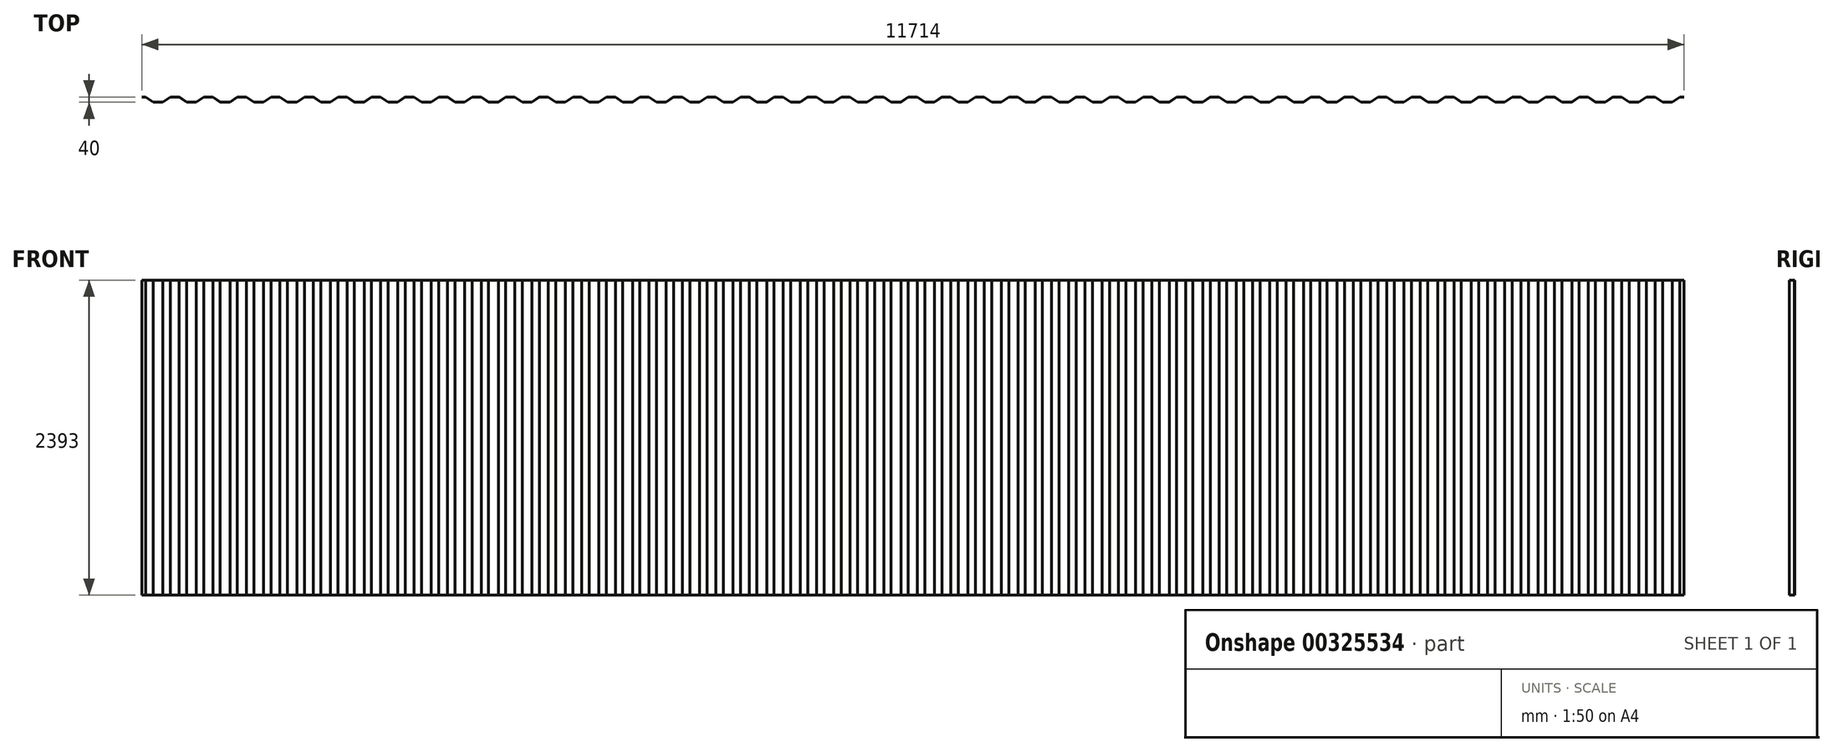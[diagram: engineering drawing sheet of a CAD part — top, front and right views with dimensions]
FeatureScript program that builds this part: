
annotation { "Feature Type Name" : "Feature", "Feature Type Description" : "" }
export const myFeature = defineFeature(function(context is Context, id is Id, definition is map)
    precondition{}
    {
        {
            var Q0;
            Q0=qCreatedBy(makeId("Top.planeOp"),FACE);
            var sketch = newSketch(context, id + "F0", { "sketchPlane" : qUnion([Q0])});
            skLineSegment(sketch, "E0", {"start": v(-32, 17.21) * mm, "end": v(-1.35, 17.21) * mm});
            skLineSegment(sketch, "E1", {"start": v(-1.35, 17.21) * mm, "end": v(55.04, -20.79) * mm});
            skLineSegment(sketch, "E2", {"start": v(55.04, -20.79) * mm, "end": v(127.96, -20.79) * mm});
            skLineSegment(sketch, "E3", {"start": v(127.96, -20.79) * mm, "end": v(184.35, 17.21) * mm});
            skLineSegment(sketch, "E4", {"start": v(184.35, 17.21) * mm, "end": v(253.44, 17.21) * mm});
            skLineSegment(sketch, "E5", {"start": v(253.44, 17.21) * mm, "end": v(309.83, -20.79) * mm});
            skLineSegment(sketch, "E6", {"start": v(309.83, -20.79) * mm, "end": v(382.74, -20.79) * mm});
            skLineSegment(sketch, "E7", {"start": v(382.74, -20.79) * mm, "end": v(439.14, 17.21) * mm});
            skLineSegment(sketch, "E8", {"start": v(439.14, 17.21) * mm, "end": v(508.22, 17.21) * mm});
            skLineSegment(sketch, "E9", {"start": v(508.22, 17.21) * mm, "end": v(564.61, -20.79) * mm});
            skLineSegment(sketch, "E10", {"start": v(564.61, -20.79) * mm, "end": v(637.53, -20.79) * mm});
            skLineSegment(sketch, "E11", {"start": v(637.53, -20.79) * mm, "end": v(693.92, 17.21) * mm});
            skLineSegment(sketch, "E12", {"start": v(693.92, 17.21) * mm, "end": v(763, 17.21) * mm});
            skLineSegment(sketch, "E13", {"start": v(763, 17.21) * mm, "end": v(819.4, -20.79) * mm});
            skLineSegment(sketch, "E14", {"start": v(819.4, -20.79) * mm, "end": v(892.31, -20.79) * mm});
            skLineSegment(sketch, "E15", {"start": v(892.31, -20.79) * mm, "end": v(948.7, 17.21) * mm});
            skLineSegment(sketch, "E16", {"start": v(948.7, 17.21) * mm, "end": v(1017.79, 17.21) * mm});
            skLineSegment(sketch, "E17", {"start": v(1017.79, 17.21) * mm, "end": v(1074.18, -20.79) * mm});
            skLineSegment(sketch, "E18", {"start": v(1074.18, -20.79) * mm, "end": v(1147.1, -20.79) * mm});
            skLineSegment(sketch, "E19", {"start": v(1147.1, -20.79) * mm, "end": v(1203.48, 17.21) * mm});
            skLineSegment(sketch, "E20", {"start": v(1203.48, 17.21) * mm, "end": v(1272.57, 17.21) * mm});
            skLineSegment(sketch, "E21", {"start": v(1272.57, 17.21) * mm, "end": v(1328.96, -20.79) * mm});
            skLineSegment(sketch, "E22", {"start": v(1328.96, -20.79) * mm, "end": v(1401.88, -20.79) * mm});
            skLineSegment(sketch, "E23", {"start": v(1401.88, -20.79) * mm, "end": v(1458.27, 17.21) * mm});
            skLineSegment(sketch, "E24", {"start": v(1458.27, 17.21) * mm, "end": v(1527.35, 17.21) * mm});
            skLineSegment(sketch, "E25", {"start": v(1527.35, 17.21) * mm, "end": v(1583.74, -20.79) * mm});
            skLineSegment(sketch, "E26", {"start": v(1583.74, -20.79) * mm, "end": v(1656.66, -20.79) * mm});
            skLineSegment(sketch, "E27", {"start": v(1656.66, -20.79) * mm, "end": v(1713.05, 17.21) * mm});
            skLineSegment(sketch, "E28", {"start": v(1713.05, 17.21) * mm, "end": v(1782.13, 17.21) * mm});
            skLineSegment(sketch, "E29", {"start": v(1782.13, 17.21) * mm, "end": v(1838.53, -20.79) * mm});
            skLineSegment(sketch, "E30", {"start": v(1838.53, -20.79) * mm, "end": v(1911.44, -20.79) * mm});
            skLineSegment(sketch, "E31", {"start": v(1911.44, -20.79) * mm, "end": v(1967.83, 17.21) * mm});
            skLineSegment(sketch, "E32", {"start": v(1967.83, 17.21) * mm, "end": v(2036.92, 17.21) * mm});
            skLineSegment(sketch, "E33", {"start": v(2036.92, 17.21) * mm, "end": v(2093.3, -20.79) * mm});
            skLineSegment(sketch, "E34", {"start": v(2093.3, -20.79) * mm, "end": v(2166.22, -20.79) * mm});
            skLineSegment(sketch, "E35", {"start": v(2166.22, -20.79) * mm, "end": v(2222.62, 17.21) * mm});
            skLineSegment(sketch, "E36", {"start": v(2222.62, 17.21) * mm, "end": v(2291.7, 17.21) * mm});
            skLineSegment(sketch, "E37", {"start": v(2291.7, 17.21) * mm, "end": v(2348.1, -20.79) * mm});
            skLineSegment(sketch, "E38", {"start": v(2348.1, -20.79) * mm, "end": v(2421, -20.79) * mm});
            skLineSegment(sketch, "E39", {"start": v(2421, -20.79) * mm, "end": v(2477.4, 17.21) * mm});
            skLineSegment(sketch, "E40", {"start": v(2477.4, 17.21) * mm, "end": v(2546.48, 17.21) * mm});
            skLineSegment(sketch, "E41", {"start": v(2546.48, 17.21) * mm, "end": v(2602.87, -20.79) * mm});
            skLineSegment(sketch, "E42", {"start": v(2602.87, -20.79) * mm, "end": v(2675.8, -20.79) * mm});
            skLineSegment(sketch, "E43", {"start": v(2675.8, -20.79) * mm, "end": v(2732.18, 17.21) * mm});
            skLineSegment(sketch, "E44", {"start": v(2732.18, 17.21) * mm, "end": v(2801.27, 17.21) * mm});
            skLineSegment(sketch, "E45", {"start": v(2801.27, 17.21) * mm, "end": v(2857.66, -20.79) * mm});
            skLineSegment(sketch, "E46", {"start": v(2857.66, -20.79) * mm, "end": v(2930.57, -20.79) * mm});
            skLineSegment(sketch, "E47", {"start": v(2930.57, -20.79) * mm, "end": v(2986.97, 17.21) * mm});
            skLineSegment(sketch, "E48", {"start": v(2986.97, 17.21) * mm, "end": v(3056.05, 17.21) * mm});
            skLineSegment(sketch, "E49", {"start": v(3056.05, 17.21) * mm, "end": v(3112.44, -20.79) * mm});
            skLineSegment(sketch, "E50", {"start": v(3112.44, -20.79) * mm, "end": v(3185.36, -20.79) * mm});
            skLineSegment(sketch, "E51", {"start": v(3185.36, -20.79) * mm, "end": v(3241.75, 17.21) * mm});
            skLineSegment(sketch, "E52", {"start": v(3241.75, 17.21) * mm, "end": v(3310.83, 17.21) * mm});
            skLineSegment(sketch, "E53", {"start": v(3310.83, 17.21) * mm, "end": v(3367.22, -20.79) * mm});
            skLineSegment(sketch, "E54", {"start": v(3367.22, -20.79) * mm, "end": v(3440.14, -20.79) * mm});
            skLineSegment(sketch, "E55", {"start": v(3440.14, -20.79) * mm, "end": v(3496.53, 17.21) * mm});
            skLineSegment(sketch, "E56", {"start": v(3496.53, 17.21) * mm, "end": v(3565.61, 17.21) * mm});
            skLineSegment(sketch, "E57", {"start": v(3565.61, 17.21) * mm, "end": v(3622, -20.79) * mm});
            skLineSegment(sketch, "E58", {"start": v(3622, -20.79) * mm, "end": v(3694.92, -20.79) * mm});
            skLineSegment(sketch, "E59", {"start": v(3694.92, -20.79) * mm, "end": v(3751.31, 17.21) * mm});
            skLineSegment(sketch, "E60", {"start": v(3751.31, 17.21) * mm, "end": v(3820.4, 17.21) * mm});
            skLineSegment(sketch, "E61", {"start": v(3820.4, 17.21) * mm, "end": v(3876.79, -20.79) * mm});
            skLineSegment(sketch, "E62", {"start": v(3876.79, -20.79) * mm, "end": v(3949.7, -20.79) * mm});
            skLineSegment(sketch, "E63", {"start": v(3949.7, -20.79) * mm, "end": v(4006.1, 17.21) * mm});
            skLineSegment(sketch, "E64", {"start": v(4006.1, 17.21) * mm, "end": v(4075.18, 17.21) * mm});
            skLineSegment(sketch, "E65", {"start": v(4075.18, 17.21) * mm, "end": v(4131.57, -20.79) * mm});
            skLineSegment(sketch, "E66", {"start": v(4131.57, -20.79) * mm, "end": v(4204.49, -20.79) * mm});
            skLineSegment(sketch, "E67", {"start": v(4204.49, -20.79) * mm, "end": v(4260.88, 17.21) * mm});
            skLineSegment(sketch, "E68", {"start": v(4260.88, 17.21) * mm, "end": v(4329.96, 17.21) * mm});
            skLineSegment(sketch, "E69", {"start": v(4329.96, 17.21) * mm, "end": v(4386.36, -20.79) * mm});
            skLineSegment(sketch, "E70", {"start": v(4386.36, -20.79) * mm, "end": v(4459.27, -20.79) * mm});
            skLineSegment(sketch, "E71", {"start": v(4459.27, -20.79) * mm, "end": v(4515.66, 17.21) * mm});
            skLineSegment(sketch, "E72", {"start": v(4515.66, 17.21) * mm, "end": v(4584.75, 17.21) * mm});
            skLineSegment(sketch, "E73", {"start": v(4584.75, 17.21) * mm, "end": v(4641.14, -20.79) * mm});
            skLineSegment(sketch, "E74", {"start": v(4641.14, -20.79) * mm, "end": v(4714.05, -20.79) * mm});
            skLineSegment(sketch, "E75", {"start": v(4714.05, -20.79) * mm, "end": v(4770.45, 17.21) * mm});
            skLineSegment(sketch, "E76", {"start": v(4770.45, 17.21) * mm, "end": v(4839.53, 17.21) * mm});
            skLineSegment(sketch, "E77", {"start": v(4839.53, 17.21) * mm, "end": v(4895.92, -20.79) * mm});
            skLineSegment(sketch, "E78", {"start": v(4895.92, -20.79) * mm, "end": v(4968.84, -20.79) * mm});
            skLineSegment(sketch, "E79", {"start": v(4968.84, -20.79) * mm, "end": v(5025.23, 17.21) * mm});
            skLineSegment(sketch, "E80", {"start": v(5025.23, 17.21) * mm, "end": v(5094.31, 17.21) * mm});
            skLineSegment(sketch, "E81", {"start": v(5094.31, 17.21) * mm, "end": v(5150.7, -20.79) * mm});
            skLineSegment(sketch, "E82", {"start": v(5150.7, -20.79) * mm, "end": v(5223.62, -20.79) * mm});
            skLineSegment(sketch, "E83", {"start": v(5223.62, -20.79) * mm, "end": v(5280.01, 17.21) * mm});
            skLineSegment(sketch, "E84", {"start": v(5280.01, 17.21) * mm, "end": v(5349.1, 17.21) * mm});
            skLineSegment(sketch, "E85", {"start": v(5349.1, 17.21) * mm, "end": v(5405.49, -20.79) * mm});
            skLineSegment(sketch, "E86", {"start": v(5405.49, -20.79) * mm, "end": v(5478.4, -20.79) * mm});
            skLineSegment(sketch, "E87", {"start": v(5478.4, -20.79) * mm, "end": v(5534.8, 17.21) * mm});
            skLineSegment(sketch, "E88", {"start": v(5534.8, 17.21) * mm, "end": v(5603.88, 17.21) * mm});
            skLineSegment(sketch, "E89", {"start": v(5603.88, 17.21) * mm, "end": v(5660.27, -20.79) * mm});
            skLineSegment(sketch, "E90", {"start": v(5660.27, -20.79) * mm, "end": v(5733.19, -20.79) * mm});
            skLineSegment(sketch, "E91", {"start": v(5733.19, -20.79) * mm, "end": v(5789.58, 17.21) * mm});
            skLineSegment(sketch, "E92", {"start": v(5789.58, 17.21) * mm, "end": v(5858.66, 17.21) * mm});
            skLineSegment(sketch, "E93", {"start": v(5858.66, 17.21) * mm, "end": v(5915.05, -20.79) * mm});
            skLineSegment(sketch, "E94", {"start": v(5915.05, -20.79) * mm, "end": v(5987.97, -20.79) * mm});
            skLineSegment(sketch, "E95", {"start": v(5987.97, -20.79) * mm, "end": v(6044.36, 17.21) * mm});
            skLineSegment(sketch, "E96", {"start": v(6044.36, 17.21) * mm, "end": v(6113.44, 17.21) * mm});
            skLineSegment(sketch, "E97", {"start": v(6113.44, 17.21) * mm, "end": v(6169.84, -20.79) * mm});
            skLineSegment(sketch, "E98", {"start": v(6169.84, -20.79) * mm, "end": v(6242.75, -20.79) * mm});
            skLineSegment(sketch, "E99", {"start": v(6242.75, -20.79) * mm, "end": v(6299.14, 17.21) * mm});
            skLineSegment(sketch, "E100", {"start": v(6299.14, 17.21) * mm, "end": v(6368.23, 17.21) * mm});
            skLineSegment(sketch, "E101", {"start": v(6368.23, 17.21) * mm, "end": v(6424.62, -20.79) * mm});
            skLineSegment(sketch, "E102", {"start": v(6424.62, -20.79) * mm, "end": v(6497.54, -20.79) * mm});
            skLineSegment(sketch, "E103", {"start": v(6497.54, -20.79) * mm, "end": v(6553.93, 17.21) * mm});
            skLineSegment(sketch, "E104", {"start": v(6553.93, 17.21) * mm, "end": v(6623.01, 17.21) * mm});
            skLineSegment(sketch, "E105", {"start": v(6623.01, 17.21) * mm, "end": v(6679.4, -20.79) * mm});
            skLineSegment(sketch, "E106", {"start": v(6679.4, -20.79) * mm, "end": v(6752.32, -20.79) * mm});
            skLineSegment(sketch, "E107", {"start": v(6752.32, -20.79) * mm, "end": v(6808.71, 17.21) * mm});
            skLineSegment(sketch, "E108", {"start": v(6808.71, 17.21) * mm, "end": v(6877.8, 17.21) * mm});
            skLineSegment(sketch, "E109", {"start": v(6877.8, 17.21) * mm, "end": v(6934.19, -20.79) * mm});
            skLineSegment(sketch, "E110", {"start": v(6934.19, -20.79) * mm, "end": v(7007.1, -20.79) * mm});
            skLineSegment(sketch, "E111", {"start": v(7007.1, -20.79) * mm, "end": v(7063.5, 17.21) * mm});
            skLineSegment(sketch, "E112", {"start": v(7063.5, 17.21) * mm, "end": v(7132.58, 17.21) * mm});
            skLineSegment(sketch, "E113", {"start": v(7132.58, 17.21) * mm, "end": v(7188.97, -20.79) * mm});
            skLineSegment(sketch, "E114", {"start": v(7188.97, -20.79) * mm, "end": v(7261.88, -20.79) * mm});
            skLineSegment(sketch, "E115", {"start": v(7261.88, -20.79) * mm, "end": v(7318.28, 17.21) * mm});
            skLineSegment(sketch, "E116", {"start": v(7318.28, 17.21) * mm, "end": v(7387.36, 17.21) * mm});
            skLineSegment(sketch, "E117", {"start": v(7387.36, 17.21) * mm, "end": v(7443.75, -20.79) * mm});
            skLineSegment(sketch, "E118", {"start": v(7443.75, -20.79) * mm, "end": v(7516.67, -20.79) * mm});
            skLineSegment(sketch, "E119", {"start": v(7516.67, -20.79) * mm, "end": v(7573.06, 17.21) * mm});
            skLineSegment(sketch, "E120", {"start": v(7573.06, 17.21) * mm, "end": v(7642.14, 17.21) * mm});
            skLineSegment(sketch, "E121", {"start": v(7642.14, 17.21) * mm, "end": v(7698.53, -20.79) * mm});
            skLineSegment(sketch, "E122", {"start": v(7698.53, -20.79) * mm, "end": v(7771.45, -20.79) * mm});
            skLineSegment(sketch, "E123", {"start": v(7771.45, -20.79) * mm, "end": v(7827.84, 17.21) * mm});
            skLineSegment(sketch, "E124", {"start": v(7827.84, 17.21) * mm, "end": v(7896.93, 17.21) * mm});
            skLineSegment(sketch, "E125", {"start": v(7896.93, 17.21) * mm, "end": v(7953.32, -20.79) * mm});
            skLineSegment(sketch, "E126", {"start": v(7953.32, -20.79) * mm, "end": v(8026.23, -20.79) * mm});
            skLineSegment(sketch, "E127", {"start": v(8026.23, -20.79) * mm, "end": v(8082.62, 17.21) * mm});
            skLineSegment(sketch, "E128", {"start": v(8082.62, 17.21) * mm, "end": v(8151.7, 17.21) * mm});
            skLineSegment(sketch, "E129", {"start": v(8151.7, 17.21) * mm, "end": v(8208.1, -20.79) * mm});
            skLineSegment(sketch, "E130", {"start": v(8208.1, -20.79) * mm, "end": v(8281.02, -20.79) * mm});
            skLineSegment(sketch, "E131", {"start": v(8281.02, -20.79) * mm, "end": v(8337.4, 17.21) * mm});
            skLineSegment(sketch, "E132", {"start": v(8337.4, 17.21) * mm, "end": v(8406.5, 17.21) * mm});
            skLineSegment(sketch, "E133", {"start": v(8406.5, 17.21) * mm, "end": v(8462.88, -20.79) * mm});
            skLineSegment(sketch, "E134", {"start": v(8462.88, -20.79) * mm, "end": v(8535.8, -20.79) * mm});
            skLineSegment(sketch, "E135", {"start": v(8535.8, -20.79) * mm, "end": v(8592.2, 17.21) * mm});
            skLineSegment(sketch, "E136", {"start": v(8592.2, 17.21) * mm, "end": v(8661.27, 17.21) * mm});
            skLineSegment(sketch, "E137", {"start": v(8661.27, 17.21) * mm, "end": v(8717.67, -20.79) * mm});
            skLineSegment(sketch, "E138", {"start": v(8717.67, -20.79) * mm, "end": v(8790.58, -20.79) * mm});
            skLineSegment(sketch, "E139", {"start": v(8790.58, -20.79) * mm, "end": v(8846.97, 17.21) * mm});
            skLineSegment(sketch, "E140", {"start": v(8846.97, 17.21) * mm, "end": v(8916.06, 17.21) * mm});
            skLineSegment(sketch, "E141", {"start": v(8916.06, 17.21) * mm, "end": v(8972.45, -20.79) * mm});
            skLineSegment(sketch, "E142", {"start": v(8972.45, -20.79) * mm, "end": v(9045.37, -20.79) * mm});
            skLineSegment(sketch, "E143", {"start": v(9045.37, -20.79) * mm, "end": v(9101.76, 17.21) * mm});
            skLineSegment(sketch, "E144", {"start": v(9101.76, 17.21) * mm, "end": v(9170.84, 17.21) * mm});
            skLineSegment(sketch, "E145", {"start": v(9170.84, 17.21) * mm, "end": v(9227.23, -20.79) * mm});
            skLineSegment(sketch, "E146", {"start": v(9227.23, -20.79) * mm, "end": v(9300.15, -20.79) * mm});
            skLineSegment(sketch, "E147", {"start": v(9300.15, -20.79) * mm, "end": v(9356.54, 17.21) * mm});
            skLineSegment(sketch, "E148", {"start": v(9356.54, 17.21) * mm, "end": v(9425.62, 17.21) * mm});
            skLineSegment(sketch, "E149", {"start": v(9425.62, 17.21) * mm, "end": v(9482.01, -20.79) * mm});
            skLineSegment(sketch, "E150", {"start": v(9482.01, -20.79) * mm, "end": v(9554.93, -20.79) * mm});
            skLineSegment(sketch, "E151", {"start": v(9554.93, -20.79) * mm, "end": v(9611.32, 17.21) * mm});
            skLineSegment(sketch, "E152", {"start": v(9611.32, 17.21) * mm, "end": v(9680.4, 17.21) * mm});
            skLineSegment(sketch, "E153", {"start": v(9680.4, 17.21) * mm, "end": v(9736.8, -20.79) * mm});
            skLineSegment(sketch, "E154", {"start": v(9736.8, -20.79) * mm, "end": v(9809.71, -20.79) * mm});
            skLineSegment(sketch, "E155", {"start": v(9809.71, -20.79) * mm, "end": v(9866.1, 17.21) * mm});
            skLineSegment(sketch, "E156", {"start": v(9866.1, 17.21) * mm, "end": v(9935.19, 17.21) * mm});
            skLineSegment(sketch, "E157", {"start": v(9935.19, 17.21) * mm, "end": v(9991.58, -20.79) * mm});
            skLineSegment(sketch, "E158", {"start": v(9991.58, -20.79) * mm, "end": v(10064.5, -20.79) * mm});
            skLineSegment(sketch, "E159", {"start": v(10064.5, -20.79) * mm, "end": v(10120.89, 17.21) * mm});
            skLineSegment(sketch, "E160", {"start": v(10120.89, 17.21) * mm, "end": v(10189.97, 17.21) * mm});
            skLineSegment(sketch, "E161", {"start": v(10189.97, 17.21) * mm, "end": v(10246.36, -20.79) * mm});
            skLineSegment(sketch, "E162", {"start": v(10246.36, -20.79) * mm, "end": v(10319.28, -20.79) * mm});
            skLineSegment(sketch, "E163", {"start": v(10319.28, -20.79) * mm, "end": v(10375.67, 17.21) * mm});
            skLineSegment(sketch, "E164", {"start": v(10375.67, 17.21) * mm, "end": v(10444.76, 17.21) * mm});
            skLineSegment(sketch, "E165", {"start": v(10444.76, 17.21) * mm, "end": v(10501.15, -20.79) * mm});
            skLineSegment(sketch, "E166", {"start": v(10501.15, -20.79) * mm, "end": v(10574.06, -20.79) * mm});
            skLineSegment(sketch, "E167", {"start": v(10574.06, -20.79) * mm, "end": v(10630.45, 17.21) * mm});
            skLineSegment(sketch, "E168", {"start": v(10630.45, 17.21) * mm, "end": v(10699.54, 17.21) * mm});
            skLineSegment(sketch, "E169", {"start": v(10699.54, 17.21) * mm, "end": v(10755.93, -20.79) * mm});
            skLineSegment(sketch, "E170", {"start": v(10755.93, -20.79) * mm, "end": v(10828.85, -20.79) * mm});
            skLineSegment(sketch, "E171", {"start": v(10828.85, -20.79) * mm, "end": v(10885.24, 17.21) * mm});
            skLineSegment(sketch, "E172", {"start": v(10885.24, 17.21) * mm, "end": v(10954.32, 17.21) * mm});
            skLineSegment(sketch, "E173", {"start": v(10954.32, 17.21) * mm, "end": v(11010.71, -20.79) * mm});
            skLineSegment(sketch, "E174", {"start": v(11010.71, -20.79) * mm, "end": v(11083.63, -20.79) * mm});
            skLineSegment(sketch, "E175", {"start": v(11083.63, -20.79) * mm, "end": v(11140.02, 17.21) * mm});
            skLineSegment(sketch, "E176", {"start": v(11140.02, 17.21) * mm, "end": v(11209.1, 17.21) * mm});
            skLineSegment(sketch, "E177", {"start": v(11209.1, 17.21) * mm, "end": v(11265.5, -20.79) * mm});
            skLineSegment(sketch, "E178", {"start": v(11265.5, -20.79) * mm, "end": v(11338.41, -20.79) * mm});
            skLineSegment(sketch, "E179", {"start": v(11338.41, -20.79) * mm, "end": v(11394.8, 17.21) * mm});
            skLineSegment(sketch, "E180", {"start": v(11394.8, 17.21) * mm, "end": v(11463.89, 17.21) * mm});
            skLineSegment(sketch, "E181", {"start": v(11463.89, 17.21) * mm, "end": v(11520.28, -20.79) * mm});
            skLineSegment(sketch, "E182", {"start": v(11520.28, -20.79) * mm, "end": v(11593.2, -20.79) * mm});
            skLineSegment(sketch, "E183", {"start": v(11593.2, -20.79) * mm, "end": v(11649.59, 17.21) * mm});
            skLineSegment(sketch, "E184", {"start": v(11649.59, 17.21) * mm, "end": v(11682, 17.21) * mm});
            skLineSegment(sketch, "E185.0", {"start": v(11650.2, 15.21) * mm, "end": v(11682, 15.21) * mm});
            skLineSegment(sketch, "E185.1", {"start": v(11593.8, -22.79) * mm, "end": v(11650.2, 15.21) * mm});
            skLineSegment(sketch, "E185.2", {"start": v(11519.67, -22.79) * mm, "end": v(11593.8, -22.79) * mm});
            skLineSegment(sketch, "E185.3", {"start": v(11463.28, 15.21) * mm, "end": v(11519.67, -22.79) * mm});
            skLineSegment(sketch, "E185.4", {"start": v(11395.41, 15.21) * mm, "end": v(11463.28, 15.21) * mm});
            skLineSegment(sketch, "E185.5", {"start": v(11339.02, -22.79) * mm, "end": v(11395.41, 15.21) * mm});
            skLineSegment(sketch, "E185.6", {"start": v(11264.88, -22.79) * mm, "end": v(11339.02, -22.79) * mm});
            skLineSegment(sketch, "E185.7", {"start": v(11208.5, 15.21) * mm, "end": v(11264.88, -22.79) * mm});
            skLineSegment(sketch, "E185.8", {"start": v(11140.63, 15.21) * mm, "end": v(11208.5, 15.21) * mm});
            skLineSegment(sketch, "E185.9", {"start": v(11084.24, -22.79) * mm, "end": v(11140.63, 15.21) * mm});
            skLineSegment(sketch, "E185.10", {"start": v(11010.1, -22.79) * mm, "end": v(11084.24, -22.79) * mm});
            skLineSegment(sketch, "E185.11", {"start": v(10953.71, 15.21) * mm, "end": v(11010.1, -22.79) * mm});
            skLineSegment(sketch, "E185.12", {"start": v(10885.85, 15.21) * mm, "end": v(10953.71, 15.21) * mm});
            skLineSegment(sketch, "E185.13", {"start": v(10829.46, -22.79) * mm, "end": v(10885.85, 15.21) * mm});
            skLineSegment(sketch, "E185.14", {"start": v(10755.32, -22.79) * mm, "end": v(10829.46, -22.79) * mm});
            skLineSegment(sketch, "E185.15", {"start": v(10698.93, 15.21) * mm, "end": v(10755.32, -22.79) * mm});
            skLineSegment(sketch, "E185.16", {"start": v(10631.07, 15.21) * mm, "end": v(10698.93, 15.21) * mm});
            skLineSegment(sketch, "E185.17", {"start": v(10574.67, -22.79) * mm, "end": v(10631.07, 15.21) * mm});
            skLineSegment(sketch, "E185.18", {"start": v(10500.54, -22.79) * mm, "end": v(10574.67, -22.79) * mm});
            skLineSegment(sketch, "E185.19", {"start": v(10444.14, 15.21) * mm, "end": v(10500.54, -22.79) * mm});
            skLineSegment(sketch, "E185.20", {"start": v(10376.28, 15.21) * mm, "end": v(10444.14, 15.21) * mm});
            skLineSegment(sketch, "E185.21", {"start": v(10319.9, -22.79) * mm, "end": v(10376.28, 15.21) * mm});
            skLineSegment(sketch, "E185.22", {"start": v(10245.75, -22.79) * mm, "end": v(10319.9, -22.79) * mm});
            skLineSegment(sketch, "E185.23", {"start": v(10189.36, 15.21) * mm, "end": v(10245.75, -22.79) * mm});
            skLineSegment(sketch, "E185.24", {"start": v(10121.5, 15.21) * mm, "end": v(10189.36, 15.21) * mm});
            skLineSegment(sketch, "E185.25", {"start": v(10065.1, -22.79) * mm, "end": v(10121.5, 15.21) * mm});
            skLineSegment(sketch, "E185.26", {"start": v(9990.97, -22.79) * mm, "end": v(10065.1, -22.79) * mm});
            skLineSegment(sketch, "E185.27", {"start": v(9934.58, 15.21) * mm, "end": v(9990.97, -22.79) * mm});
            skLineSegment(sketch, "E185.28", {"start": v(9866.72, 15.21) * mm, "end": v(9934.58, 15.21) * mm});
            skLineSegment(sketch, "E185.29", {"start": v(9810.33, -22.79) * mm, "end": v(9866.72, 15.21) * mm});
            skLineSegment(sketch, "E185.30", {"start": v(9736.19, -22.79) * mm, "end": v(9810.33, -22.79) * mm});
            skLineSegment(sketch, "E185.31", {"start": v(9679.8, 15.21) * mm, "end": v(9736.19, -22.79) * mm});
            skLineSegment(sketch, "E185.32", {"start": v(9611.93, 15.21) * mm, "end": v(9679.8, 15.21) * mm});
            skLineSegment(sketch, "E185.33", {"start": v(9555.54, -22.79) * mm, "end": v(9611.93, 15.21) * mm});
            skLineSegment(sketch, "E185.34", {"start": v(9481.4, -22.79) * mm, "end": v(9555.54, -22.79) * mm});
            skLineSegment(sketch, "E185.35", {"start": v(9425.01, 15.21) * mm, "end": v(9481.4, -22.79) * mm});
            skLineSegment(sketch, "E185.36", {"start": v(9357.15, 15.21) * mm, "end": v(9425.01, 15.21) * mm});
            skLineSegment(sketch, "E185.37", {"start": v(9300.76, -22.79) * mm, "end": v(9357.15, 15.21) * mm});
            skLineSegment(sketch, "E185.38", {"start": v(9226.62, -22.79) * mm, "end": v(9300.76, -22.79) * mm});
            skLineSegment(sketch, "E185.39", {"start": v(9170.23, 15.21) * mm, "end": v(9226.62, -22.79) * mm});
            skLineSegment(sketch, "E185.40", {"start": v(9102.37, 15.21) * mm, "end": v(9170.23, 15.21) * mm});
            skLineSegment(sketch, "E185.41", {"start": v(9045.98, -22.79) * mm, "end": v(9102.37, 15.21) * mm});
            skLineSegment(sketch, "E185.42", {"start": v(8971.84, -22.79) * mm, "end": v(9045.98, -22.79) * mm});
            skLineSegment(sketch, "E185.43", {"start": v(8915.45, 15.21) * mm, "end": v(8971.84, -22.79) * mm});
            skLineSegment(sketch, "E185.44", {"start": v(8847.58, 15.21) * mm, "end": v(8915.45, 15.21) * mm});
            skLineSegment(sketch, "E185.45", {"start": v(8791.2, -22.79) * mm, "end": v(8847.58, 15.21) * mm});
            skLineSegment(sketch, "E185.46", {"start": v(8717.05, -22.79) * mm, "end": v(8791.2, -22.79) * mm});
            skLineSegment(sketch, "E185.47", {"start": v(8660.66, 15.21) * mm, "end": v(8717.05, -22.79) * mm});
            skLineSegment(sketch, "E185.48", {"start": v(8592.8, 15.21) * mm, "end": v(8660.66, 15.21) * mm});
            skLineSegment(sketch, "E185.49", {"start": v(8536.41, -22.79) * mm, "end": v(8592.8, 15.21) * mm});
            skLineSegment(sketch, "E185.50", {"start": v(8462.27, -22.79) * mm, "end": v(8536.41, -22.79) * mm});
            skLineSegment(sketch, "E185.51", {"start": v(8405.88, 15.21) * mm, "end": v(8462.27, -22.79) * mm});
            skLineSegment(sketch, "E185.52", {"start": v(8338.02, 15.21) * mm, "end": v(8405.88, 15.21) * mm});
            skLineSegment(sketch, "E185.53", {"start": v(8281.63, -22.79) * mm, "end": v(8338.02, 15.21) * mm});
            skLineSegment(sketch, "E185.54", {"start": v(8207.49, -22.79) * mm, "end": v(8281.63, -22.79) * mm});
            skLineSegment(sketch, "E185.55", {"start": v(8151.1, 15.21) * mm, "end": v(8207.49, -22.79) * mm});
            skLineSegment(sketch, "E185.56", {"start": v(8083.24, 15.21) * mm, "end": v(8151.1, 15.21) * mm});
            skLineSegment(sketch, "E185.57", {"start": v(8026.84, -22.79) * mm, "end": v(8083.24, 15.21) * mm});
            skLineSegment(sketch, "E185.58", {"start": v(7952.7, -22.79) * mm, "end": v(8026.84, -22.79) * mm});
            skLineSegment(sketch, "E185.59", {"start": v(7896.31, 15.21) * mm, "end": v(7952.7, -22.79) * mm});
            skLineSegment(sketch, "E185.60", {"start": v(7828.45, 15.21) * mm, "end": v(7896.31, 15.21) * mm});
            skLineSegment(sketch, "E185.61", {"start": v(7772.06, -22.79) * mm, "end": v(7828.45, 15.21) * mm});
            skLineSegment(sketch, "E185.62", {"start": v(7697.92, -22.79) * mm, "end": v(7772.06, -22.79) * mm});
            skLineSegment(sketch, "E185.63", {"start": v(7641.53, 15.21) * mm, "end": v(7697.92, -22.79) * mm});
            skLineSegment(sketch, "E185.64", {"start": v(7573.67, 15.21) * mm, "end": v(7641.53, 15.21) * mm});
            skLineSegment(sketch, "E185.65", {"start": v(7517.28, -22.79) * mm, "end": v(7573.67, 15.21) * mm});
            skLineSegment(sketch, "E185.66", {"start": v(7443.14, -22.79) * mm, "end": v(7517.28, -22.79) * mm});
            skLineSegment(sketch, "E185.67", {"start": v(7386.75, 15.21) * mm, "end": v(7443.14, -22.79) * mm});
            skLineSegment(sketch, "E185.68", {"start": v(7318.89, 15.21) * mm, "end": v(7386.75, 15.21) * mm});
            skLineSegment(sketch, "E185.69", {"start": v(7262.5, -22.79) * mm, "end": v(7318.89, 15.21) * mm});
            skLineSegment(sketch, "E185.70", {"start": v(7188.36, -22.79) * mm, "end": v(7262.5, -22.79) * mm});
            skLineSegment(sketch, "E185.71", {"start": v(7131.97, 15.21) * mm, "end": v(7188.36, -22.79) * mm});
            skLineSegment(sketch, "E185.72", {"start": v(7064.1, 15.21) * mm, "end": v(7131.97, 15.21) * mm});
            skLineSegment(sketch, "E185.73", {"start": v(7007.71, -22.79) * mm, "end": v(7064.1, 15.21) * mm});
            skLineSegment(sketch, "E185.74", {"start": v(6933.57, -22.79) * mm, "end": v(7007.71, -22.79) * mm});
            skLineSegment(sketch, "E185.75", {"start": v(6877.18, 15.21) * mm, "end": v(6933.57, -22.79) * mm});
            skLineSegment(sketch, "E185.76", {"start": v(6809.32, 15.21) * mm, "end": v(6877.18, 15.21) * mm});
            skLineSegment(sketch, "E185.77", {"start": v(6752.93, -22.79) * mm, "end": v(6809.32, 15.21) * mm});
            skLineSegment(sketch, "E185.78", {"start": v(6678.8, -22.79) * mm, "end": v(6752.93, -22.79) * mm});
            skLineSegment(sketch, "E185.79", {"start": v(6622.4, 15.21) * mm, "end": v(6678.8, -22.79) * mm});
            skLineSegment(sketch, "E185.80", {"start": v(6554.54, 15.21) * mm, "end": v(6622.4, 15.21) * mm});
            skLineSegment(sketch, "E185.81", {"start": v(6498.15, -22.79) * mm, "end": v(6554.54, 15.21) * mm});
            skLineSegment(sketch, "E185.82", {"start": v(6424, -22.79) * mm, "end": v(6498.15, -22.79) * mm});
            skLineSegment(sketch, "E185.83", {"start": v(6367.62, 15.21) * mm, "end": v(6424, -22.79) * mm});
            skLineSegment(sketch, "E185.84", {"start": v(6299.76, 15.21) * mm, "end": v(6367.62, 15.21) * mm});
            skLineSegment(sketch, "E185.85", {"start": v(6243.36, -22.79) * mm, "end": v(6299.76, 15.21) * mm});
            skLineSegment(sketch, "E185.86", {"start": v(6169.23, -22.79) * mm, "end": v(6243.36, -22.79) * mm});
            skLineSegment(sketch, "E185.87", {"start": v(6112.83, 15.21) * mm, "end": v(6169.23, -22.79) * mm});
            skLineSegment(sketch, "E185.88", {"start": v(6044.97, 15.21) * mm, "end": v(6112.83, 15.21) * mm});
            skLineSegment(sketch, "E185.89", {"start": v(2800.65, 15.21) * mm, "end": v(2857.05, -22.79) * mm});
            skLineSegment(sketch, "E185.90", {"start": v(2732.8, 15.21) * mm, "end": v(2800.65, 15.21) * mm});
            skLineSegment(sketch, "E185.91", {"start": v(2676.4, -22.79) * mm, "end": v(2732.8, 15.21) * mm});
            skLineSegment(sketch, "E185.92", {"start": v(2602.26, -22.79) * mm, "end": v(2676.4, -22.79) * mm});
            skLineSegment(sketch, "E185.93", {"start": v(2545.87, 15.21) * mm, "end": v(2602.26, -22.79) * mm});
            skLineSegment(sketch, "E185.94", {"start": v(2478.01, 15.21) * mm, "end": v(2545.87, 15.21) * mm});
            skLineSegment(sketch, "E185.95", {"start": v(2421.62, -22.79) * mm, "end": v(2478.01, 15.21) * mm});
            skLineSegment(sketch, "E185.96", {"start": v(2347.48, -22.79) * mm, "end": v(2421.62, -22.79) * mm});
            skLineSegment(sketch, "E185.97", {"start": v(2291.09, 15.21) * mm, "end": v(2347.48, -22.79) * mm});
            skLineSegment(sketch, "E185.98", {"start": v(2223.23, 15.21) * mm, "end": v(2291.09, 15.21) * mm});
            skLineSegment(sketch, "E185.99", {"start": v(2166.84, -22.79) * mm, "end": v(2223.23, 15.21) * mm});
            skLineSegment(sketch, "E185.100", {"start": v(2092.7, -22.79) * mm, "end": v(2166.84, -22.79) * mm});
            skLineSegment(sketch, "E185.101", {"start": v(2036.3, 15.21) * mm, "end": v(2092.7, -22.79) * mm});
            skLineSegment(sketch, "E185.102", {"start": v(1968.44, 15.21) * mm, "end": v(2036.3, 15.21) * mm});
            skLineSegment(sketch, "E185.103", {"start": v(1912.05, -22.79) * mm, "end": v(1968.44, 15.21) * mm});
            skLineSegment(sketch, "E185.104", {"start": v(1837.91, -22.79) * mm, "end": v(1912.05, -22.79) * mm});
            skLineSegment(sketch, "E185.105", {"start": v(1781.52, 15.21) * mm, "end": v(1837.91, -22.79) * mm});
            skLineSegment(sketch, "E185.106", {"start": v(1713.66, 15.21) * mm, "end": v(1781.52, 15.21) * mm});
            skLineSegment(sketch, "E185.107", {"start": v(1657.27, -22.79) * mm, "end": v(1713.66, 15.21) * mm});
            skLineSegment(sketch, "E185.108", {"start": v(1583.13, -22.79) * mm, "end": v(1657.27, -22.79) * mm});
            skLineSegment(sketch, "E185.109", {"start": v(1526.74, 15.21) * mm, "end": v(1583.13, -22.79) * mm});
            skLineSegment(sketch, "E185.110", {"start": v(1458.88, 15.21) * mm, "end": v(1526.74, 15.21) * mm});
            skLineSegment(sketch, "E185.111", {"start": v(1402.49, -22.79) * mm, "end": v(1458.88, 15.21) * mm});
            skLineSegment(sketch, "E185.112", {"start": v(1328.35, -22.79) * mm, "end": v(1402.49, -22.79) * mm});
            skLineSegment(sketch, "E185.113", {"start": v(507.6, 15.21) * mm, "end": v(564, -22.79) * mm});
            skLineSegment(sketch, "E185.114", {"start": v(439.75, 15.21) * mm, "end": v(507.6, 15.21) * mm});
            skLineSegment(sketch, "E185.115", {"start": v(383.36, -22.79) * mm, "end": v(439.75, 15.21) * mm});
            skLineSegment(sketch, "E185.116", {"start": v(309.22, -22.79) * mm, "end": v(383.36, -22.79) * mm});
            skLineSegment(sketch, "E185.117", {"start": v(252.83, 15.21) * mm, "end": v(309.22, -22.79) * mm});
            skLineSegment(sketch, "E185.118", {"start": v(184.96, 15.21) * mm, "end": v(252.83, 15.21) * mm});
            skLineSegment(sketch, "E185.119", {"start": v(-32, 15.21) * mm, "end": v(-1.96, 15.21) * mm});
            skLineSegment(sketch, "E185.120", {"start": v(-1.96, 15.21) * mm, "end": v(54.43, -22.79) * mm});
            skLineSegment(sketch, "E185.121", {"start": v(54.43, -22.79) * mm, "end": v(128.57, -22.79) * mm});
            skLineSegment(sketch, "E185.122", {"start": v(128.57, -22.79) * mm, "end": v(184.96, 15.21) * mm});
            skLineSegment(sketch, "E185.123", {"start": v(564, -22.79) * mm, "end": v(638.14, -22.79) * mm});
            skLineSegment(sketch, "E185.124", {"start": v(638.14, -22.79) * mm, "end": v(694.53, 15.21) * mm});
            skLineSegment(sketch, "E185.125", {"start": v(694.53, 15.21) * mm, "end": v(762.4, 15.21) * mm});
            skLineSegment(sketch, "E185.126", {"start": v(762.4, 15.21) * mm, "end": v(818.78, -22.79) * mm});
            skLineSegment(sketch, "E185.127", {"start": v(818.78, -22.79) * mm, "end": v(892.92, -22.79) * mm});
            skLineSegment(sketch, "E185.128", {"start": v(892.92, -22.79) * mm, "end": v(949.31, 15.21) * mm});
            skLineSegment(sketch, "E185.129", {"start": v(949.31, 15.21) * mm, "end": v(1017.17, 15.21) * mm});
            skLineSegment(sketch, "E185.130", {"start": v(1017.17, 15.21) * mm, "end": v(1073.57, -22.79) * mm});
            skLineSegment(sketch, "E185.131", {"start": v(1073.57, -22.79) * mm, "end": v(1147.7, -22.79) * mm});
            skLineSegment(sketch, "E185.132", {"start": v(1147.7, -22.79) * mm, "end": v(1204.1, 15.21) * mm});
            skLineSegment(sketch, "E185.133", {"start": v(1204.1, 15.21) * mm, "end": v(1271.96, 15.21) * mm});
            skLineSegment(sketch, "E185.134", {"start": v(1271.96, 15.21) * mm, "end": v(1328.35, -22.79) * mm});
            skLineSegment(sketch, "E185.135", {"start": v(2857.05, -22.79) * mm, "end": v(2931.18, -22.79) * mm});
            skLineSegment(sketch, "E185.136", {"start": v(2931.18, -22.79) * mm, "end": v(2987.58, 15.21) * mm});
            skLineSegment(sketch, "E185.137", {"start": v(2987.58, 15.21) * mm, "end": v(3055.44, 15.21) * mm});
            skLineSegment(sketch, "E185.138", {"start": v(3055.44, 15.21) * mm, "end": v(3111.83, -22.79) * mm});
            skLineSegment(sketch, "E185.139", {"start": v(3111.83, -22.79) * mm, "end": v(3185.97, -22.79) * mm});
            skLineSegment(sketch, "E185.140", {"start": v(3185.97, -22.79) * mm, "end": v(3242.36, 15.21) * mm});
            skLineSegment(sketch, "E185.141", {"start": v(3242.36, 15.21) * mm, "end": v(3310.22, 15.21) * mm});
            skLineSegment(sketch, "E185.142", {"start": v(3310.22, 15.21) * mm, "end": v(3366.61, -22.79) * mm});
            skLineSegment(sketch, "E185.143", {"start": v(3366.61, -22.79) * mm, "end": v(3440.75, -22.79) * mm});
            skLineSegment(sketch, "E185.144", {"start": v(3440.75, -22.79) * mm, "end": v(3497.14, 15.21) * mm});
            skLineSegment(sketch, "E185.145", {"start": v(3497.14, 15.21) * mm, "end": v(3565, 15.21) * mm});
            skLineSegment(sketch, "E185.146", {"start": v(3565, 15.21) * mm, "end": v(3621.4, -22.79) * mm});
            skLineSegment(sketch, "E185.147", {"start": v(3621.4, -22.79) * mm, "end": v(3695.53, -22.79) * mm});
            skLineSegment(sketch, "E185.148", {"start": v(3695.53, -22.79) * mm, "end": v(3751.93, 15.21) * mm});
            skLineSegment(sketch, "E185.149", {"start": v(3751.93, 15.21) * mm, "end": v(3819.79, 15.21) * mm});
            skLineSegment(sketch, "E185.150", {"start": v(3819.79, 15.21) * mm, "end": v(3876.18, -22.79) * mm});
            skLineSegment(sketch, "E185.151", {"start": v(3876.18, -22.79) * mm, "end": v(3950.32, -22.79) * mm});
            skLineSegment(sketch, "E185.152", {"start": v(3950.32, -22.79) * mm, "end": v(4006.7, 15.21) * mm});
            skLineSegment(sketch, "E185.153", {"start": v(4006.7, 15.21) * mm, "end": v(4074.57, 15.21) * mm});
            skLineSegment(sketch, "E185.154", {"start": v(4074.57, 15.21) * mm, "end": v(4130.96, -22.79) * mm});
            skLineSegment(sketch, "E185.155", {"start": v(4130.96, -22.79) * mm, "end": v(4205.1, -22.79) * mm});
            skLineSegment(sketch, "E185.156", {"start": v(4205.1, -22.79) * mm, "end": v(4261.5, 15.21) * mm});
            skLineSegment(sketch, "E185.157", {"start": v(4261.5, 15.21) * mm, "end": v(4329.35, 15.21) * mm});
            skLineSegment(sketch, "E185.158", {"start": v(4329.35, 15.21) * mm, "end": v(4385.74, -22.79) * mm});
            skLineSegment(sketch, "E185.159", {"start": v(4385.74, -22.79) * mm, "end": v(4459.88, -22.79) * mm});
            skLineSegment(sketch, "E185.160", {"start": v(4459.88, -22.79) * mm, "end": v(4516.27, 15.21) * mm});
            skLineSegment(sketch, "E185.161", {"start": v(4516.27, 15.21) * mm, "end": v(4584.14, 15.21) * mm});
            skLineSegment(sketch, "E185.162", {"start": v(4584.14, 15.21) * mm, "end": v(4640.53, -22.79) * mm});
            skLineSegment(sketch, "E185.163", {"start": v(4640.53, -22.79) * mm, "end": v(4714.67, -22.79) * mm});
            skLineSegment(sketch, "E185.164", {"start": v(4714.67, -22.79) * mm, "end": v(4771.06, 15.21) * mm});
            skLineSegment(sketch, "E185.165", {"start": v(4771.06, 15.21) * mm, "end": v(4838.92, 15.21) * mm});
            skLineSegment(sketch, "E185.166", {"start": v(4838.92, 15.21) * mm, "end": v(4895.31, -22.79) * mm});
            skLineSegment(sketch, "E185.167", {"start": v(4895.31, -22.79) * mm, "end": v(4969.45, -22.79) * mm});
            skLineSegment(sketch, "E185.168", {"start": v(4969.45, -22.79) * mm, "end": v(5025.84, 15.21) * mm});
            skLineSegment(sketch, "E185.169", {"start": v(5025.84, 15.21) * mm, "end": v(5093.7, 15.21) * mm});
            skLineSegment(sketch, "E185.170", {"start": v(5093.7, 15.21) * mm, "end": v(5150.1, -22.79) * mm});
            skLineSegment(sketch, "E185.171", {"start": v(5150.1, -22.79) * mm, "end": v(5224.23, -22.79) * mm});
            skLineSegment(sketch, "E185.172", {"start": v(5224.23, -22.79) * mm, "end": v(5280.62, 15.21) * mm});
            skLineSegment(sketch, "E185.173", {"start": v(5280.62, 15.21) * mm, "end": v(5348.48, 15.21) * mm});
            skLineSegment(sketch, "E185.174", {"start": v(5348.48, 15.21) * mm, "end": v(5404.88, -22.79) * mm});
            skLineSegment(sketch, "E185.175", {"start": v(5404.88, -22.79) * mm, "end": v(5479.01, -22.79) * mm});
            skLineSegment(sketch, "E185.176", {"start": v(5479.01, -22.79) * mm, "end": v(5535.4, 15.21) * mm});
            skLineSegment(sketch, "E185.177", {"start": v(5535.4, 15.21) * mm, "end": v(5603.27, 15.21) * mm});
            skLineSegment(sketch, "E185.178", {"start": v(5603.27, 15.21) * mm, "end": v(5659.66, -22.79) * mm});
            skLineSegment(sketch, "E185.179", {"start": v(5659.66, -22.79) * mm, "end": v(5733.8, -22.79) * mm});
            skLineSegment(sketch, "E185.180", {"start": v(5733.8, -22.79) * mm, "end": v(5790.19, 15.21) * mm});
            skLineSegment(sketch, "E185.181", {"start": v(5790.19, 15.21) * mm, "end": v(5858.05, 15.21) * mm});
            skLineSegment(sketch, "E185.182", {"start": v(5858.05, 15.21) * mm, "end": v(5914.44, -22.79) * mm});
            skLineSegment(sketch, "E185.183", {"start": v(5914.44, -22.79) * mm, "end": v(5988.58, -22.79) * mm});
            skLineSegment(sketch, "E185.184", {"start": v(5988.58, -22.79) * mm, "end": v(6044.97, 15.21) * mm});
            skLineSegment(sketch, "E186", {"start": v(-32, 17.21) * mm, "end": v(-32, 15.21) * mm});
            skLineSegment(sketch, "E187", {"start": v(11682, 17.21) * mm, "end": v(11682, 15.21) * mm});
            skSolve(sketch);
        }
        {
            var Q0;
            Q0=makeQuery(id+"F0.imprint","IMPRINT",FACE,{"disambiguationData":[TD([[makeQuery(id+"F0.imprint","IMPRINT",EDGE,{"derivedFrom":sQuery(id+"F0.wireOp",EDGE,"E0")}),-1.0]])]});
            extrude(context, id + "F1", {"entities" : qUnion([Q0]), "depth" : 2393 * mm});
        }
    });
